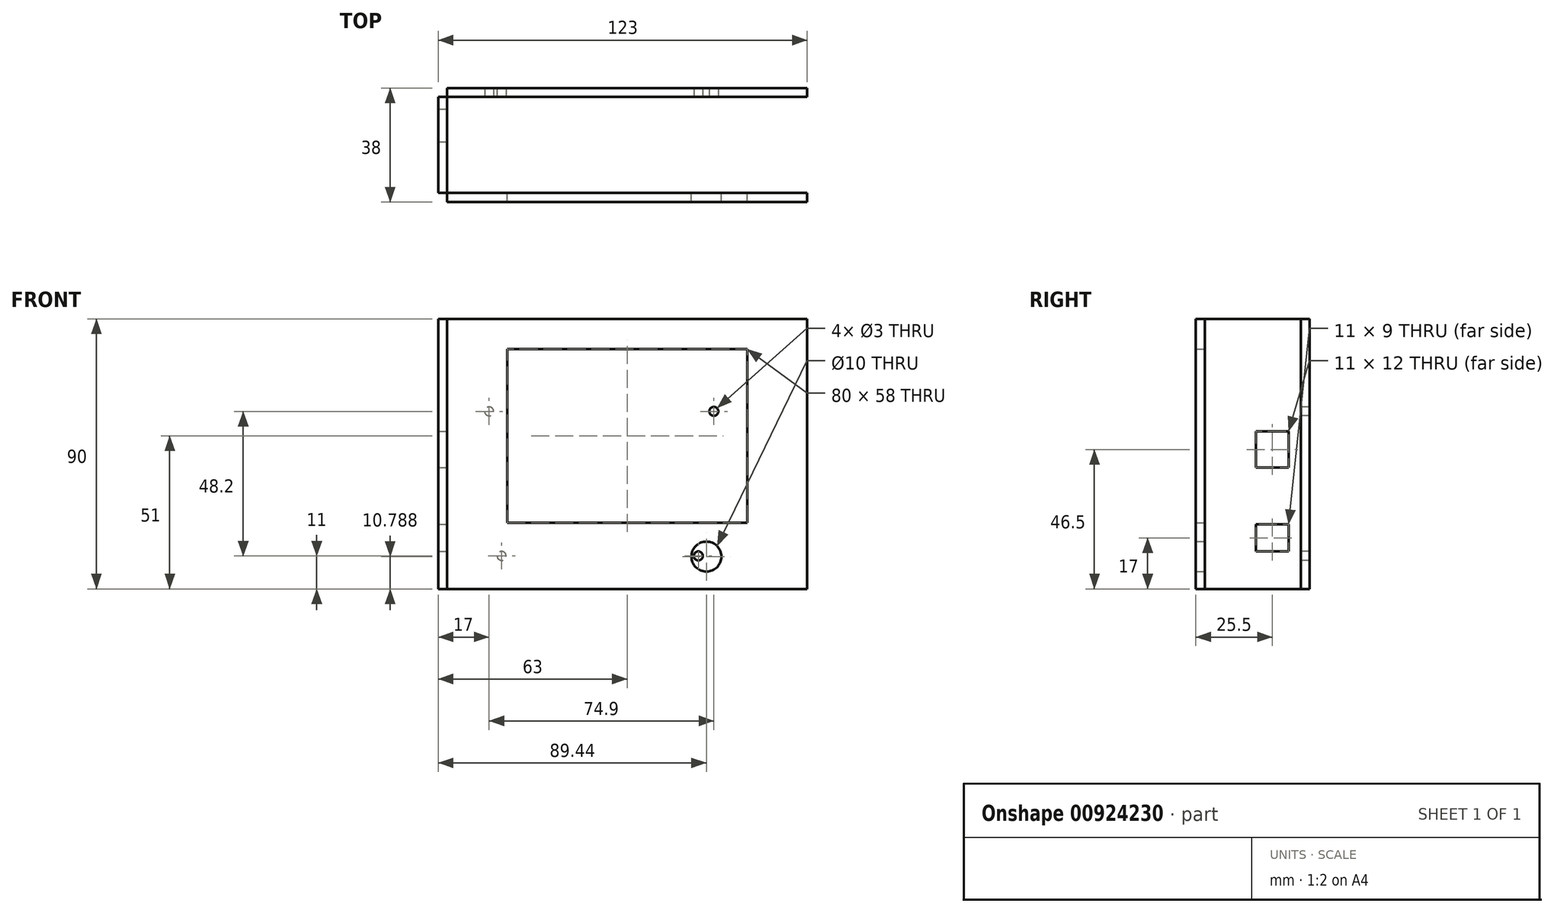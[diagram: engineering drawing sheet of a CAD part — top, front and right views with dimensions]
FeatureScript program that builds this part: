
annotation { "Feature Type Name" : "Feature", "Feature Type Description" : "" }
export const myFeature = defineFeature(function(context is Context, id is Id, definition is map)
    precondition{}
    {
        {
            var Q0;
            Q0=qCreatedBy(makeId("Front.planeOp"),FACE);
            var sketch = newSketch(context, id + "F0", { "sketchPlane" : qUnion([Q0])});
            skLineSegment(sketch, "E0.bottom", {"start": v(-50, 42) * mm, "end": v(-130, 42) * mm});
            skLineSegment(sketch, "E0.top", {"start": v(-50, 100) * mm, "end": v(-130, 100) * mm});
            skLineSegment(sketch, "E0.left", {"start": v(-50, 42) * mm, "end": v(-50, 100) * mm});
            skLineSegment(sketch, "E0.right", {"start": v(-130, 42) * mm, "end": v(-130, 100) * mm});
            skPoint(sketch, "E0.middle", {"position": v(-90, 71) * mm});
            skLineSegment(sketch, "E1.bottom", {"start": v(-30, 20) * mm, "end": v(-150, 20) * mm});
            skLineSegment(sketch, "E1.top", {"start": v(-30, 110) * mm, "end": v(-150, 110) * mm});
            skLineSegment(sketch, "E1.left", {"start": v(-30, 20) * mm, "end": v(-30, 110) * mm});
            skLineSegment(sketch, "E1.right", {"start": v(-150, 20) * mm, "end": v(-150, 110) * mm});
            skPoint(sketch, "E1.middle", {"position": v(-90, 65) * mm});
            skCircle(sketch, "E2", {"center": v(-63.56, 30.79) * mm, "radius": 5 * mm});
            skSolve(sketch);
        }
        {
            var Q0;
            Q0=qCreatedBy(makeId("Right.planeOp"),FACE);
            cPlane(context, id + "F1", {"entities" : qUnion([Q0]), "cplaneType" : CPlaneType.OFFSET, "offset" : 150 * mm, "oppositeDirection" : true, "width" : 150 * mm, "height" : 150 * mm});
        }
        {
            var Q0;
            Q0=qCreatedBy(id+"F1.planeOp",FACE);
            var sketch = newSketch(context, id + "F2", { "sketchPlane" : qUnion([Q0])});
            skLineSegment(sketch, "E3.bottom", {"start": v(28, 32.5) * mm, "end": v(17, 32.5) * mm});
            skLineSegment(sketch, "E3.top", {"start": v(28, 41.5) * mm, "end": v(17, 41.5) * mm});
            skLineSegment(sketch, "E3.left", {"start": v(28, 32.5) * mm, "end": v(28, 41.5) * mm});
            skLineSegment(sketch, "E3.right", {"start": v(17, 32.5) * mm, "end": v(17, 41.5) * mm});
            skPoint(sketch, "E3.middle", {"position": v(22.5, 37) * mm});
            skPoint(sketch, "E4", {"position": v(28, 31.25) * mm});
            skLineSegment(sketch, "E5.bottom", {"start": v(28, 60.5) * mm, "end": v(17, 60.5) * mm});
            skLineSegment(sketch, "E5.top", {"start": v(28, 72.5) * mm, "end": v(17, 72.5) * mm});
            skLineSegment(sketch, "E5.left", {"start": v(28, 60.5) * mm, "end": v(28, 72.5) * mm});
            skLineSegment(sketch, "E5.right", {"start": v(17, 60.5) * mm, "end": v(17, 72.5) * mm});
            skPoint(sketch, "E5.middle", {"position": v(22.5, 66.5) * mm});
            skLineSegment(sketch, "E6.bottom", {"start": v(32, 110) * mm, "end": v(0, 110) * mm});
            skLineSegment(sketch, "E6.top", {"start": v(32, 20) * mm, "end": v(0, 20) * mm});
            skLineSegment(sketch, "E6.left", {"start": v(32, 110) * mm, "end": v(32, 20) * mm});
            skLineSegment(sketch, "E6.right", {"start": v(0, 110) * mm, "end": v(0, 20) * mm});
            skPoint(sketch, "E6.middle", {"position": v(16, 65) * mm});
            skSolve(sketch);
        }
        {
            var Q0;
            Q0 = qSketchRegion(id + "F2", true);
            extrude(context, id + "F3", {"entities" : qUnion([Q0]), "oppositeDirection" : true, "depth" : 3 * mm, "offsetDistance" : 25 * mm});
        }
        {
            var Q0;
            Q0=makeQuery(id+"F0.imprint","IMPRINT",FACE,{"disambiguationData":[TD([[makeQuery(id+"F0.imprint","IMPRINT",EDGE,{"derivedFrom":sQuery(id+"F0.wireOp",EDGE,"E0.bottom")}),1.0]])]});
            extrude(context, id + "F4", {"entities" : qUnion([Q0]), "depth" : 3 * mm, "offsetDistance" : 25 * mm});
        }
        {
            var Q0;
            Q0=makeQuery(id+"F3.opExtrude","SWEPT_FACE",FACE,{"disambiguationData":[OSD([sQuery(id+"F2.wireOp",EDGE,"E6.left")])]});
            var sketch = newSketch(context, id + "F5", { "sketchPlane" : qUnion([Q0])});
            skLineSegment(sketch, "E7.bottom", {"start": v(30, 110) * mm, "end": v(150, 110) * mm});
            skLineSegment(sketch, "E7.top", {"start": v(30, 20) * mm, "end": v(150, 20) * mm});
            skLineSegment(sketch, "E7.left", {"start": v(30, 110) * mm, "end": v(30, 20) * mm});
            skLineSegment(sketch, "E7.right", {"start": v(150, 110) * mm, "end": v(150, 20) * mm});
            skPoint(sketch, "E7.middle", {"position": v(90, 65) * mm});
            skLineSegment(sketch, "E8.bottom", {"start": v(48.4, 28.5) * mm, "end": v(150, 28.5) * mm});
            skLineSegment(sketch, "E8.top", {"start": v(48.4, 81.8) * mm, "end": v(150, 81.8) * mm});
            skLineSegment(sketch, "E8.left", {"start": v(48.4, 28.5) * mm, "end": v(48.4, 81.8) * mm});
            skLineSegment(sketch, "E8.right", {"start": v(150, 28.5) * mm, "end": v(150, 81.8) * mm});
            skPoint(sketch, "E8.middle", {"position": v(99.2, 55.15) * mm});
            skCircle(sketch, "E9", {"center": v(131.83, 31) * mm, "radius": 1.5 * mm});
            skCircle(sketch, "E10", {"center": v(66.26, 31) * mm, "radius": 1.5 * mm});
            skCircle(sketch, "E11", {"center": v(136, 79.2) * mm, "radius": 1.5 * mm});
            skCircle(sketch, "E12", {"center": v(61.1, 79.2) * mm, "radius": 1.5 * mm});
            skSolve(sketch);
        }
        {
            var Q0;
            {var subQ1=sQuery(id+"F5.wireOp",EDGE,"E7.bottom");Q0=makeQuery(id+"F5.imprint","IMPRINT",FACE,{"disambiguationData":[TD([[makeQuery(id+"F5.imprint","IMPRINT",EDGE,{"derivedFrom":subQ1}),-1.0]])]});}
            var Q1;
            Q1=makeQuery(id+"F5.imprint","IMPRINT",FACE,{"disambiguationData":[TD([[makeQuery(id+"F5.imprint","IMPRINT",EDGE,{"derivedFrom":sQuery(id+"F5.wireOp",EDGE,"E8.bottom")}),1.0]])]});
            extrude(context, id + "F6", {"entities" : qUnion([Q0, Q1]), "depth" : 3 * mm, "offsetDistance" : 25 * mm});
        }
    });
